# Revit family: FU_Table_Sandler_Salinero
name_source: partatom
category: Furniture
units: mm (PartAtom-declared; Revit-internal decimal feet)

## family parameters
Always vertical = Yes
Cut with Voids When Loaded = No
OmniClass Number = 23.40.20.00
OmniClass Title = General Furniture and Specialties
Room Calculation Point = No
Shared = No
Work Plane-Based = No

## types (6) — shared parameters
Depth = 1000 mm  [stored 3.28084 ft]
Description = Conference table with steel legs, and  HPL solid laminate top.
Frame = Metal - Paint -AL VR - Matt Jet Black
Height = 760 mm
Manufacturer = Sandler
Top = HPL - Solid - White
URL = https://www.sandlerseating.com
zero-valued in all types: Default Elevation

## per-type parameters (varying)
| type | Left Leg Edge | Num Cross Supports | Right Leg Edge | Width |
| Salinero 8.1 | 30 mm | 3 | 30 mm | 1000 mm  [stored 3.28084 ft] |
| Salinero 8.2 | 30 mm | 4 | 30 mm | 2000 mm  [stored 6.56168 ft] |
| Salinero 8.3 | 30 mm | 4 | 30 mm | 2400 mm |
| Salinero 8.4 | 30 mm | 4 | 30 mm | 3000 mm  [stored 9.84252 ft] |
| Salinero 8.5 | 335 mm  [stored 1.09908 ft] | 3 | 335 mm  [stored 1.09908 ft] | 2600 mm  [stored 8.53018 ft] |
| Salinero 8.6 | 335 mm  [stored 1.09908 ft] | 4 | 335 mm  [stored 1.09908 ft] | 3000 mm  [stored 9.84252 ft] |

note: column(s) folded — value = type name in every type: Model

note: [stored X ft] marks values corroborated as IEEE doubles in the binary element streams (Revit-internal decimal feet)

## geometry (parser evidence)
native form markers: Sweep x2
no freeform markers — native parametric forms only
